# Revit family: Toilet_Seat-Elongated_Closed_Front-KOHLER-C3-230-K-4108T
name_source: partatom
category: Plumbing Fixtures
revit_build: Autodesk Revit 2017 (Build: 20160225_1515(x64)
units: mm (PartAtom-declared; Revit-internal decimal feet)

## family parameters
Cut with Voids When Loaded = No
Host = Face
OmniClass Number = 23.31.19.19.17
OmniClass Title = Water Closet Seats
Part Type = Normal
Room Calculation Point = No
Round Connector Dimension = Use Diameter
Shared = No

## types (1)
- 0-White
    ADA Compliant = No
    Apparent Load = 2400 VA
    Assembly Code = C1030200
    CW Connection = Yes
    Cold Water Inlet = Cold Water Inlet
    Date Modified = 12/22/2020
    Default Elevation = 0"
    Description = Qingshubao Smart Toilet Cover
    Electrical Connector = Yes
    Electrical Note = Route the electrical and install to a 220-240V GFCI- or ELCB-protected Receptacle
    Finish = Kohler-Plastic-0-White
    HW Connection = No
    Height = 6 3/16"
    Length = 20 1/2"
    Manufacturer = KOHLER Co.
    MasterFormat 1995 = 10820
    MasterFormat 2004 = 10.28.13
    Material = Plastic
    Model = K-4108T-0
    Product Documentation Link = https://files.kohler.com.cn
    Product Name = C3-230
    Product Page URL = https://www.kohler.com.cn
    URL = http://www.kohler.com.cn
    Vent Connection = No
    Voltage = 240 V
    Waste Connection = No
    WaterSense Certified = No
    Width = 17 1/8"

## geometry (parser evidence)
native form markers: Sweep x6
no freeform markers — native parametric forms only
